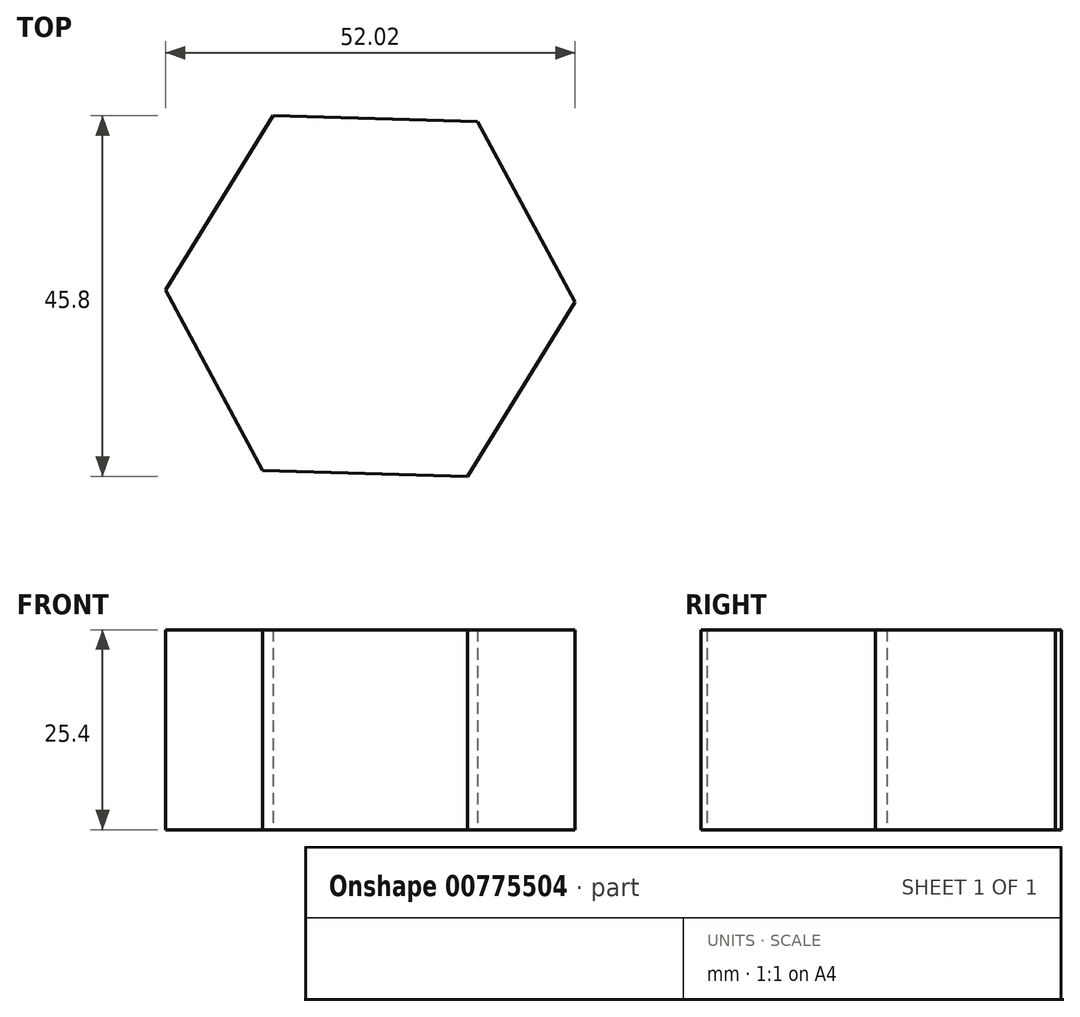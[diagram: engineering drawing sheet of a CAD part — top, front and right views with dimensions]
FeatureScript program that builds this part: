
annotation { "Feature Type Name" : "Feature", "Feature Type Description" : "" }
export const myFeature = defineFeature(function(context is Context, id is Id, definition is map)
    precondition{}
    {
        {
            var Q0;
            Q0=qCreatedBy(makeId("Top.planeOp"),FACE);
            var sketch = newSketch(context, id + "F0", { "sketchPlane" : qUnion([Q0])});
            skCircle(sketch, "E0.cCircle", {"center": v(0, 0) * mm, "radius": 26.02 * mm, "construction": true});
            skLineSegment(sketch, "E0.0", {"start": v(12.35, -22.9) * mm, "end": v(-13.66, -22.15) * mm});
            skLineSegment(sketch, "E0.1", {"start": v(-13.66, -22.15) * mm, "end": v(-26, 0.75) * mm});
            skLineSegment(sketch, "E0.2", {"start": v(-26, 0.75) * mm, "end": v(-12.35, 22.9) * mm});
            skLineSegment(sketch, "E0.3", {"start": v(-12.35, 22.9) * mm, "end": v(13.66, 22.15) * mm});
            skLineSegment(sketch, "E0.4", {"start": v(13.66, 22.15) * mm, "end": v(26, -0.75) * mm});
            skLineSegment(sketch, "E0.5", {"start": v(26, -0.75) * mm, "end": v(12.35, -22.9) * mm});
            skSolve(sketch);
        }
        {
            var Q0;
            Q0=makeQuery(id+"F0.imprint","IMPRINT",FACE,{"disambiguationData":[TD([[makeQuery(id+"F0.imprint","IMPRINT",EDGE,{"derivedFrom":sQuery(id+"F0.wireOp",EDGE,"E0.0")}),-1.0]])]});
            extrude(context, id + "F1", {"entities" : qUnion([Q0]), "depth" : 25.4 * mm, "offsetDistance" : 25.4 * mm});
        }
    });
